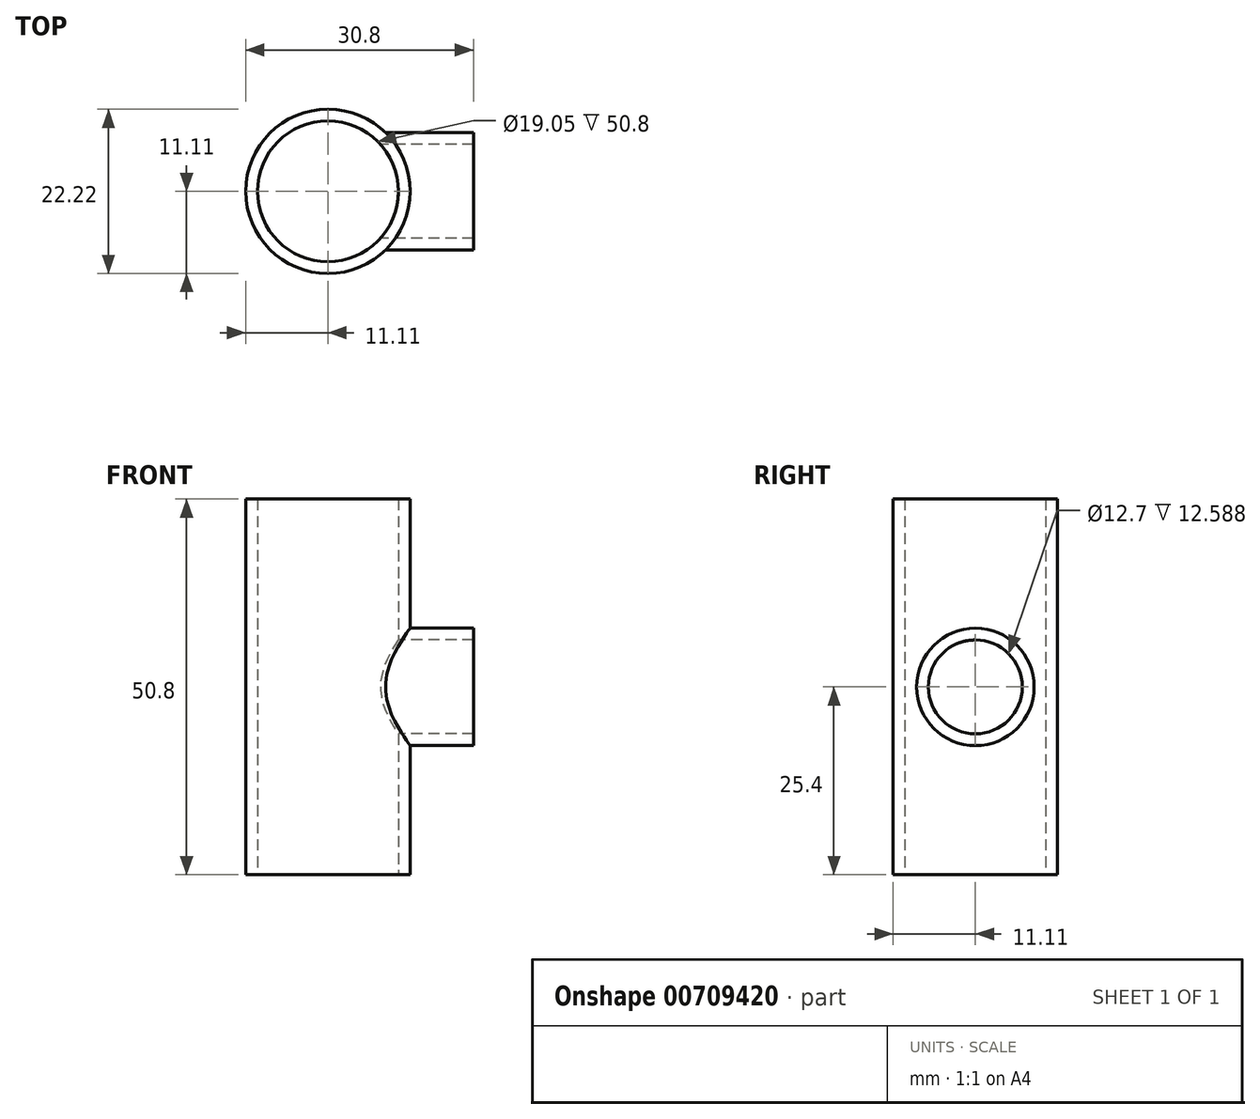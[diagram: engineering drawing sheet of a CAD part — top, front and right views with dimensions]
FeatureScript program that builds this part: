
annotation { "Feature Type Name" : "Feature", "Feature Type Description" : "" }
export const myFeature = defineFeature(function(context is Context, id is Id, definition is map)
    precondition{}
    {
        {
            var Q0;
            Q0=qCreatedBy(makeId("Top.planeOp"),FACE);
            var sketch = newSketch(context, id + "F0", { "sketchPlane" : qUnion([Q0])});
            skLineSegment(sketch, "E0", {"start": v(0, 0) * mm, "end": v(9.53, 0) * mm});
            skCircle(sketch, "E1", {"center": v(0, 0) * mm, "radius": 9.53 * mm});
            skCircle(sketch, "E2.0", {"center": v(0, 0) * mm, "radius": 11.11 * mm});
            skSolve(sketch);
        }
        {
            var Q0;
            Q0=makeQuery(id+"F0.imprint","IMPRINT",FACE,{"disambiguationData":[TD([[makeQuery(id+"F0.imprint","IMPRINT",EDGE,{"derivedFrom":sQuery(id+"F0.wireOp",EDGE,"E1")}),-1.0]])]});
            extrude(context, id + "F1", {"entities" : qUnion([Q0]), "depth" : 25.4 * mm, "offsetDistance" : 25.4 * mm, "hasSecondDirection" : true, "secondDirectionOppositeDirection" : true, "secondDirectionDepth" : 25.4 * mm});
        }
        {
            var Q0;
            Q0=qCreatedBy(makeId("Right.planeOp"),FACE);
            var sketch = newSketch(context, id + "F2", { "sketchPlane" : qUnion([Q0])});
            skCircle(sketch, "E3", {"center": v(0, 0) * mm, "radius": 7.94 * mm});
            skCircle(sketch, "E4.0", {"center": v(0, 0) * mm, "radius": 6.35 * mm});
            skSolve(sketch);
        }
        {
            var Q0;
            Q0=makeQuery(id+"F2.imprint","IMPRINT",FACE,{"disambiguationData":[TD([[makeQuery(id+"F2.imprint","IMPRINT",EDGE,{"derivedFrom":sQuery(id+"F2.wireOp",EDGE,"E3")}),1.0]])]});
            extrude(context, id + "F3", {"entities" : qUnion([Q0]), "operationType" : NewBodyOperationType.ADD, "depth" : 19.68 * mm, "offsetDistance" : 25.4 * mm, "hasSecondDirection" : true, "secondDirectionOppositeDirection" : false, "secondDirectionDepth" : 5.08 * mm});
        }
        {
            var Q0;
            Q0=makeQuery(id+"F3.opExtrude","CAP_FACE",FACE,{"disambiguationData":[OSD([sQuery(id+"F2.wireOp",EDGE,"E3"),sQuery(id+"F2.wireOp",EDGE,"E4.0")])],"isStart":false});
            var sketch = newSketch(context, id + "F4", { "sketchPlane" : qUnion([Q0])});
            skSolve(sketch);
        }
        {
            var Q0;
            Q0=qSketchRegion(id+"F4",true);
            var Q1;
            Q1=makeQuery(id+"F4.imprint","IMPRINT",FACE,{"disambiguationData":[TD([[makeQuery(id+"F4.imprint","IMPRINT",EDGE,{"derivedFrom":makeQuery(id+"F3.opExtrude","CAP_EDGE",EDGE,{"disambiguationData":[OSD([sQuery(id+"F2.wireOp",EDGE,"E4.0")])],"isStart":false})}),1.0]])]});
            extrude(context, id + "F5", {"entities" : qUnion([Q0, Q1]), "operationType" : NewBodyOperationType.REMOVE, "oppositeDirection" : true, "depth" : 25.4 * mm, "offsetDistance" : 25.4 * mm});
        }
        {
            var Q0;
            Q0=makeQuery(id+"F1.opExtrude","CAP_FACE",FACE,{"disambiguationData":[OSD([sQuery(id+"F0.wireOp",EDGE,"E1"),sQuery(id+"F0.wireOp",EDGE,"E2.0")])],"isStart":true});
            var sketch = newSketch(context, id + "F6", { "sketchPlane" : qUnion([Q0])});
            skSolve(sketch);
        }
        {
            var Q0;
            Q0=qSketchRegion(id+"F6",true);
            var Q1;
            Q1=makeQuery(id+"F6.imprint","IMPRINT",FACE,{"disambiguationData":[TD([[makeQuery(id+"F6.imprint","IMPRINT",EDGE,{"derivedFrom":makeQuery(id+"F1.opExtrude","CAP_EDGE",EDGE,{"disambiguationData":[OSD([sQuery(id+"F0.wireOp",EDGE,"E1")])],"isStart":true})}),-1.0]])]});
            extrude(context, id + "F7", {"entities" : qUnion([Q0, Q1]), "operationType" : NewBodyOperationType.REMOVE, "oppositeDirection" : true, "depth" : 50.8 * mm, "offsetDistance" : 25.4 * mm});
        }
    });
